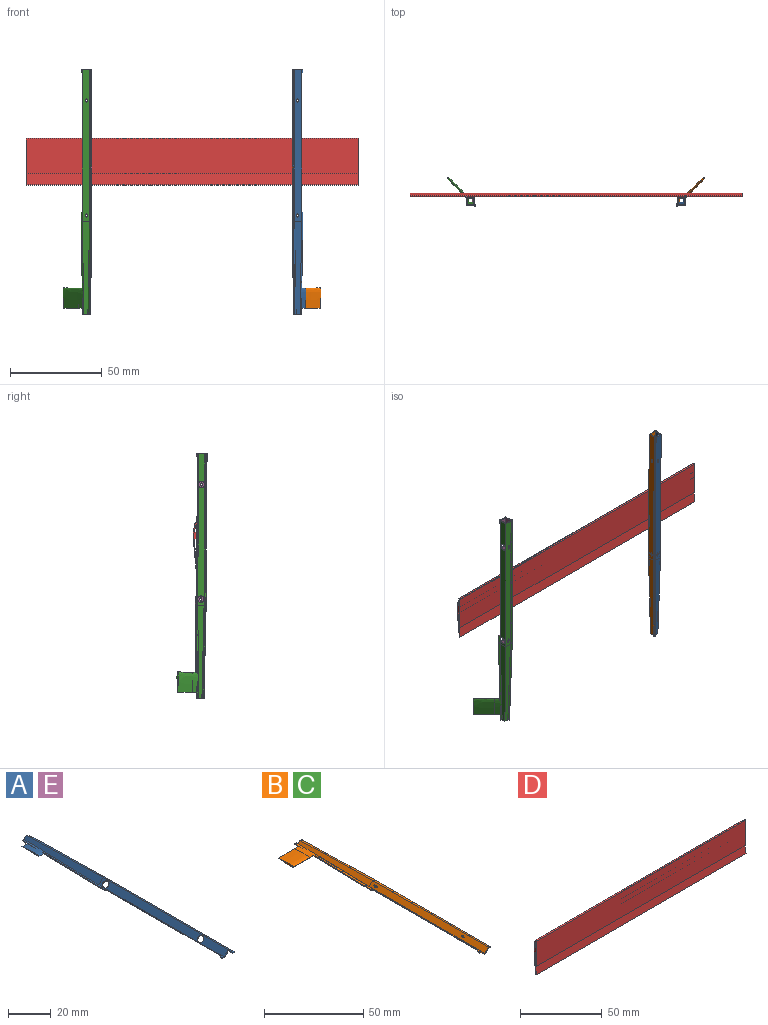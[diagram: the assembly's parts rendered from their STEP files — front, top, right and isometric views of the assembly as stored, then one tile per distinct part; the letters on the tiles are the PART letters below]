
ASSEMBLY  parts=5 mates=2
PART A: 46 faces, bbox 10.2x133.9x3.8 mm
  f0: plane 133.35x4.58mm, normal (0,0,-1), area 117.6mm2, adj f1,f6,f7,f8,f15,f26,f31,f32
  f1: plane 1.46x0.48mm, normal (-1,0,0), area 0.7mm2, adj f0,f3,f15,f38
  f2: plane 43.34x1.86mm, normal (0,0,1), area 40.5mm2, adj f6,f8,f9,f18,f30,f35,f39,f40
  f3: plane 2.67x0.95mm, normal (0,0,1), area 2mm2, adj f1,f9,f15,f38,f42,f43
  f4: cylinder r=1.81mm len=3.63mm, axis (-0.71,0,0.71), area 5.4mm2, adj f7,f9,f19,f37
  f5: plane 9.18x1.18mm, normal (0,0,1), area 8.7mm2, adj f26,f30,f31,f35
  f6: plane 37.73x1.14mm, normal (-1,0.02,0), area 17.5mm2, adj f0,f2,f8,f35
  f7: plane 82.55x2.58mm, normal (0.71,0,-0.71), area 280.9mm2, adj f0,f4,f14,f15,f17,f32
  f8: plane 4.63x0.48mm, normal (-1,0,0), area 2.2mm2, adj f0,f2,f6,f39
  f9: plane 82.55x2.78mm, normal (-0.71,0,0.71), area 303.9mm2, adj f2,f3,f4,f10,f15,f17,f30,f37
  f10: plane 82.55x2.78mm, normal (0.71,0,0.71), area 322mm2, adj f9,f11,f15,f20,f21,f22,f23,f24
  f11: plane 133.35x2.19mm, normal (0,0,1), area 127mm2, adj f10,f12,f15,f26,f28,f29
  f12: plane 82.55x0.48mm, normal (1,0,0), area 39.3mm2, adj f11,f13,f15,f28
  f13: plane 133.35x2.38mm, normal (0,0,-1), area 153.3mm2, adj f12,f14,f15,f26,f27,f28
  f14: plane 82.55x2.58mm, normal (-0.71,0,-0.71), area 299mm2, adj f7,f13,f15,f16,f19,f20,f21,f22
  f15: plane 7.46x3.26mm, normal (0,-1,0), area 4.6mm2, adj f0,f1,f3,f7,f9,f10,f11,f12
  f16: plane 1.1x0.06mm, normal (-0.71,0,0.71), area 0.1mm2, adj f14,f17
  f17: cylinder r=1.81mm len=3.63mm, axis (-0.71,0,0.71), area 5.4mm2, adj f7,f9,f16,f18
  f18: plane 1.1x0.06mm, normal (0.71,0,-0.71), area 0.1mm2, adj f2,f17
  f19: plane 1.1x0.06mm, normal (-0.71,0,0.71), area 0.1mm2, adj f4,f14
  f20: cylinder r=0.19mm len=0.6mm, axis (0.71,0,0.71), area 0.6mm2, adj f10,f14
  f21: cylinder r=0.56mm len=1.13mm, axis (0.71,0,0.71), area 1.7mm2, adj f10,f14
  f22: cylinder r=0.19mm len=0.6mm, axis (0.71,0,0.71), area 0.6mm2, adj f10,f14
  f23: cylinder r=0.19mm len=0.6mm, axis (0.71,0,0.71), area 0.6mm2, adj f10,f14
  f24: cylinder r=0.19mm len=0.6mm, axis (0.71,0,0.71), area 0.6mm2, adj f10,f14
  f25: cylinder r=0.56mm len=1.13mm, axis (0.71,0,0.71), area 1.7mm2, adj f10,f14
  f26: plane 4.99x2.02mm, normal (0,1,0), area 2.9mm2, adj f0,f5,f11,f13,f27,f28,f29,f30
  f27: plane 50.8x2.58mm, normal (-0.71,-0.02,-0.71), area 141.1mm2, adj f13,f14,f26,f32
  f28: plane 50.8x1.23mm, normal (1,0.02,0), area 24.2mm2, adj f11,f12,f13,f26
  f29: plane 50.8x2.78mm, normal (0.71,0.02,0.71), area 155.3mm2, adj f10,f11,f26,f30
  f30: plane 51.37x3.35mm, normal (-0.71,0.02,0.71), area 154.9mm2, adj f2,f5,f9,f26,f29,f35
  f31: plane 9.4x0.7mm, normal (-1,0.02,0), area 3mm2, adj f0,f5,f26,f35
  f32: plane 50.81x2.59mm, normal (0.71,-0.02,-0.71), area 140.5mm2, adj f0,f7,f26,f27,f33,f34
  f33: plane 6.31x0.15mm, normal (1,0,0), area 0.5mm2, adj f0,f32,f34
  f34: extruded ~0.15x0.15mm, area 0mm2, adj f0,f32,f33
  f35: extruded ~11.11x4.16mm, area 40.2mm2, adj f0,f2,f5,f6,f30,f31,f36
  f36: plane 11.11x1.17mm, normal (-1,0,0), area 4mm2, adj f0,f35
  f37: plane 74.2x0.65mm, normal (-1,0,0), area 35.2mm2, adj f0,f4,f9,f41,f42
  f38: cylinder r=0.32mm len=0.48mm, axis (0,0,-1), area 0.1mm2, adj f0,f1,f3,f43
  f39: cylinder r=0.32mm len=0.48mm, axis (0,0,-1), area 0.1mm2, adj f0,f2,f8,f40
  f40: plane 0.77x0.77mm, normal (-0.71,-0.71,0), area 0.5mm2, adj f0,f2,f39,f41
  f41: cylinder r=0.32mm len=0.48mm, axis (0,0,-1), area 0.1mm2, adj f0,f2,f37,f40
  f42: cylinder r=0.32mm len=0.48mm, axis (0,0,-1), area 0.1mm2, adj f0,f3,f37,f43
  f43: plane 0.77x0.77mm, normal (-0.71,0.71,0), area 0.5mm2, adj f0,f3,f38,f42
  f44: cylinder r=0.19mm len=0.48mm, axis (0,0,-1), area 0.6mm2, adj f0,f2
  f45: cylinder r=0.19mm len=0.48mm, axis (0,0,-1), area 0.6mm2, adj f0,f2
PART B: 170 faces, bbox 21.7x133.9x5 mm
  f0: plane 43.34x1.86mm, normal (0,0,-1), area 39.2mm2, adj f7,f9,f12,f13,f21,f89,f90,f91
  f1: plane 9.18x1.18mm, normal (0,0,-1), area 8.3mm2, adj f7,f8,f29,f107,f142,f143,f144,f145
  f2: plane 133.35x2.19mm, normal (0,0,-1), area 122.1mm2, adj f14,f15,f18,f29,f31,f32,f33,f34
  f3: plane 2.67x0.95mm, normal (0,0,-1), area 1.5mm2, adj f5,f13,f18,f82,f83,f84,f85,f86
  f4: plane 133.35x4.58mm, normal (0,0,1), area 117.4mm2, adj f5,f8,f9,f10,f11,f12,f18,f29
  f5: plane 1.46x0.48mm, normal (-1,0,0), area 0.7mm2, adj f3,f4,f18,f112
  f6: cylinder r=1.81mm len=3.63mm, axis (-0.71,0,-0.71), area 5.4mm2, adj f11,f13,f22,f111
  f7: plane 51.37x3.35mm, normal (-0.71,0.02,-0.71), area 154.9mm2, adj f0,f1,f13,f29,f32,f107
  f8: plane 9.4x0.7mm, normal (-1,0.02,0), area 3mm2, adj f1,f4,f29,f107
  f9: plane 37.73x1.14mm, normal (-1,0.02,0), area 17.5mm2, adj f0,f4,f12,f107
  f10: plane 50.81x2.59mm, normal (0.71,-0.02,0.71), area 140.5mm2, adj f4,f11,f29,f30,f105,f106
  f11: plane 82.55x2.58mm, normal (0.71,0,0.71), area 280.9mm2, adj f4,f6,f10,f17,f18,f20
  f12: plane 4.63x0.48mm, normal (-1,0,0), area 2.2mm2, adj f0,f4,f9,f113
  f13: plane 82.55x2.78mm, normal (-0.71,0,-0.71), area 303.9mm2, adj f0,f3,f6,f7,f14,f18,f20,f111
  f14: plane 82.55x2.78mm, normal (0.71,0,-0.71), area 322mm2, adj f2,f13,f18,f23,f24,f25,f26,f27
  f15: plane 82.55x0.48mm, normal (1,0,0), area 39.3mm2, adj f2,f16,f18,f31
  f16: plane 133.35x2.38mm, normal (0,0,1), area 152.5mm2, adj f15,f17,f18,f29,f30,f31,f96,f97
  f17: plane 82.55x2.58mm, normal (-0.71,0,0.71), area 299mm2, adj f11,f16,f18,f19,f22,f23,f24,f25
  f18: plane 7.46x3.26mm, normal (0,-1,0), area 4.6mm2, adj f2,f3,f4,f5,f11,f13,f14,f15
  f19: plane 1.1x0.06mm, normal (-0.71,0,-0.71), area 0.1mm2, adj f17,f20
  f20: cylinder r=1.81mm len=3.63mm, axis (-0.71,0,-0.71), area 5.4mm2, adj f11,f13,f19,f21
  f21: plane 1.1x0.06mm, normal (0.71,0,0.71), area 0.1mm2, adj f0,f20
  f22: plane 1.1x0.06mm, normal (-0.71,0,-0.71), area 0.1mm2, adj f6,f17
  f23: cylinder r=0.19mm len=0.6mm, axis (0.71,0,-0.71), area 0.6mm2, adj f14,f17
  f24: cylinder r=0.56mm len=1.13mm, axis (0.71,0,-0.71), area 1.7mm2, adj f14,f17
  f25: cylinder r=0.19mm len=0.6mm, axis (0.71,0,-0.71), area 0.6mm2, adj f14,f17
  f26: cylinder r=0.19mm len=0.6mm, axis (0.71,0,-0.71), area 0.6mm2, adj f14,f17
  f27: cylinder r=0.19mm len=0.6mm, axis (0.71,0,-0.71), area 0.6mm2, adj f14,f17
  f28: cylinder r=0.56mm len=1.13mm, axis (0.71,0,-0.71), area 1.7mm2, adj f14,f17
  f29: plane 4.99x2.02mm, normal (0,1,0), area 2.9mm2, adj f1,f2,f4,f7,f8,f10,f16,f30
  f30: plane 50.8x2.58mm, normal (-0.71,-0.02,0.71), area 141.1mm2, adj f10,f16,f17,f29
  f31: plane 50.8x1.23mm, normal (1,0.02,0), area 24.2mm2, adj f2,f15,f16,f29
  f32: plane 50.8x2.78mm, normal (0.71,0.02,-0.71), area 155.3mm2, adj f2,f7,f14,f29
  f33: plane 0.43x0.31mm, normal (-1,0,0), area 0.1mm2, adj f2,f34,f38,f39
  f34: plane 0.38x0.31mm, normal (-0.5,0.87,0), area 0.1mm2, adj f2,f33,f35,f39
  f35: plane 0.38x0.31mm, normal (0.5,0.87,0), area 0.1mm2, adj f2,f34,f36,f39
  f36: plane 0.43x0.31mm, normal (1,0,0), area 0.1mm2, adj f2,f35,f37,f39
  f37: plane 0.38x0.31mm, normal (0.5,-0.87,0), area 0.1mm2, adj f2,f36,f38,f39
  f38: plane 0.38x0.31mm, normal (-0.5,-0.87,0), area 0.1mm2, adj f2,f33,f37,f39
  f39: plane 0.87x0.75mm, normal (0,0,-1), area 0.4mm2, adj f33,f34,f35,f36,f37,f38,f96
  f40: plane 0.38x0.31mm, normal (0.5,-0.87,0), area 0.1mm2, adj f2,f41,f45,f46
  f41: plane 0.38x0.31mm, normal (-0.5,-0.87,0), area 0.1mm2, adj f2,f40,f42,f46
  f42: plane 0.43x0.31mm, normal (-1,0,0), area 0.1mm2, adj f2,f41,f43,f46
  f43: plane 0.38x0.31mm, normal (-0.5,0.87,0), area 0.1mm2, adj f2,f42,f44,f46
  f44: plane 0.38x0.31mm, normal (0.5,0.87,0), area 0.1mm2, adj f2,f43,f45,f46
  f45: plane 0.43x0.31mm, normal (1,0,0), area 0.1mm2, adj f2,f40,f44,f46
  f46: plane 0.87x0.75mm, normal (0,0,-1), area 0.4mm2, adj f40,f41,f42,f43,f44,f45,f102
  f47: plane 0.38x0.31mm, normal (0.5,-0.87,0), area 0.1mm2, adj f2,f48,f52,f53
  f48: plane 0.38x0.31mm, normal (-0.5,-0.87,0), area 0.1mm2, adj f2,f47,f49,f53
  f49: plane 0.43x0.31mm, normal (-1,0,0), area 0.1mm2, adj f2,f48,f50,f53
  f50: plane 0.38x0.31mm, normal (-0.5,0.87,0), area 0.1mm2, adj f2,f49,f51,f53
  f51: plane 0.38x0.31mm, normal (0.5,0.87,0), area 0.1mm2, adj f2,f50,f52,f53
  f52: plane 0.43x0.31mm, normal (1,0,0), area 0.1mm2, adj f2,f47,f51,f53
  f53: plane 0.87x0.75mm, normal (0,0,-1), area 0.4mm2, adj f47,f48,f49,f50,f51,f52,f101
  f54: plane 0.38x0.31mm, normal (0.5,-0.87,0), area 0.1mm2, adj f2,f55,f59,f60
  f55: plane 0.38x0.31mm, normal (-0.5,-0.87,0), area 0.1mm2, adj f2,f54,f56,f60
  f56: plane 0.43x0.31mm, normal (-1,0,0), area 0.1mm2, adj f2,f55,f57,f60
  f57: plane 0.38x0.31mm, normal (-0.5,0.87,0), area 0.1mm2, adj f2,f56,f58,f60
  f58: plane 0.38x0.31mm, normal (0.5,0.87,0), area 0.1mm2, adj f2,f57,f59,f60
  f59: plane 0.43x0.31mm, normal (1,0,0), area 0.1mm2, adj f2,f54,f58,f60
  f60: plane 0.87x0.75mm, normal (0,0,-1), area 0.4mm2, adj f54,f55,f56,f57,f58,f59,f100
  f61: plane 0.38x0.31mm, normal (0.5,-0.87,0), area 0.1mm2, adj f2,f62,f66,f67
  f62: plane 0.38x0.31mm, normal (-0.5,-0.87,0), area 0.1mm2, adj f2,f61,f63,f67
  f63: plane 0.43x0.31mm, normal (-1,0,0), area 0.1mm2, adj f2,f62,f64,f67
  f64: plane 0.38x0.31mm, normal (-0.5,0.87,0), area 0.1mm2, adj f2,f63,f65,f67
  f65: plane 0.38x0.31mm, normal (0.5,0.87,0), area 0.1mm2, adj f2,f64,f66,f67
  f66: plane 0.43x0.31mm, normal (1,0,0), area 0.1mm2, adj f2,f61,f65,f67
  f67: plane 0.87x0.75mm, normal (0,0,-1), area 0.4mm2, adj f61,f62,f63,f64,f65,f66,f99
  f68: plane 0.38x0.31mm, normal (0.5,-0.87,0), area 0.1mm2, adj f2,f69,f73,f74
  f69: plane 0.38x0.31mm, normal (-0.5,-0.87,0), area 0.1mm2, adj f2,f68,f70,f74
  f70: plane 0.43x0.31mm, normal (-1,0,0), area 0.1mm2, adj f2,f69,f71,f74
  f71: plane 0.38x0.31mm, normal (-0.5,0.87,0), area 0.1mm2, adj f2,f70,f72,f74
  f72: plane 0.38x0.31mm, normal (0.5,0.87,0), area 0.1mm2, adj f2,f71,f73,f74
  f73: plane 0.43x0.31mm, normal (1,0,0), area 0.1mm2, adj f2,f68,f72,f74
  f74: plane 0.87x0.75mm, normal (0,0,-1), area 0.4mm2, adj f68,f69,f70,f71,f72,f73,f98
  f75: plane 0.38x0.31mm, normal (0.5,-0.87,0), area 0.1mm2, adj f2,f76,f80,f81
  f76: plane 0.38x0.31mm, normal (-0.5,-0.87,0), area 0.1mm2, adj f2,f75,f77,f81
  f77: plane 0.43x0.31mm, normal (-1,0,0), area 0.1mm2, adj f2,f76,f78,f81
  f78: plane 0.38x0.31mm, normal (-0.5,0.87,0), area 0.1mm2, adj f2,f77,f79,f81
  f79: plane 0.38x0.31mm, normal (0.5,0.87,0), area 0.1mm2, adj f2,f78,f80,f81
  f80: plane 0.43x0.31mm, normal (1,0,0), area 0.1mm2, adj f2,f75,f79,f81
  f81: plane 0.87x0.75mm, normal (0,0,-1), area 0.4mm2, adj f75,f76,f77,f78,f79,f80,f97
  f82: plane 0.43x0.31mm, normal (-1,0,0), area 0.1mm2, adj f3,f83,f87,f88
  f83: plane 0.38x0.31mm, normal (-0.5,0.87,0), area 0.1mm2, adj f3,f82,f84,f88
  f84: plane 0.38x0.31mm, normal (0.5,0.87,0), area 0.1mm2, adj f3,f83,f85,f88
  f85: plane 0.43x0.31mm, normal (1,0,0), area 0.1mm2, adj f3,f84,f86,f88
  f86: plane 0.38x0.31mm, normal (0.5,-0.87,0), area 0.1mm2, adj f3,f85,f87,f88
  f87: plane 0.38x0.31mm, normal (-0.5,-0.87,0), area 0.1mm2, adj f3,f82,f86,f88
  f88: plane 0.87x0.75mm, normal (0,0,-1), area 0.4mm2, adj f82,f83,f84,f85,f86,f87,f103
  f89: plane 0.43x0.31mm, normal (-1,0,0), area 0.1mm2, adj f0,f90,f94,f95
  f90: plane 0.38x0.31mm, normal (-0.5,0.87,0), area 0.1mm2, adj f0,f89,f91,f95
  f91: plane 0.38x0.31mm, normal (0.5,0.87,0), area 0.1mm2, adj f0,f90,f92,f95
  f92: plane 0.43x0.31mm, normal (1,0,0), area 0.1mm2, adj f0,f91,f93,f95
  f93: plane 0.38x0.31mm, normal (0.5,-0.87,0), area 0.1mm2, adj f0,f92,f94,f95
  f94: plane 0.38x0.31mm, normal (-0.5,-0.87,0), area 0.1mm2, adj f0,f89,f93,f95
  f95: plane 0.87x0.75mm, normal (0,0,-1), area 0.4mm2, adj f89,f90,f91,f92,f93,f94,f104
  f96: cylinder r=0.19mm len=0.38mm, axis (0,0,-1), area 0.2mm2, adj f16,f39
  f97: cylinder r=0.19mm len=0.38mm, axis (0,0,-1), area 0.2mm2, adj f16,f81
  f98: cylinder r=0.19mm len=0.38mm, axis (0,0,-1), area 0.2mm2, adj f16,f74
  f99: cylinder r=0.19mm len=0.38mm, axis (0,0,-1), area 0.2mm2, adj f16,f67
  f100: cylinder r=0.19mm len=0.38mm, axis (0,0,-1), area 0.2mm2, adj f16,f60
  f101: cylinder r=0.19mm len=0.38mm, axis (0,0,-1), area 0.2mm2, adj f16,f53
  f102: cylinder r=0.19mm len=0.38mm, axis (0,0,-1), area 0.2mm2, adj f16,f46
  f103: cylinder r=0.19mm len=0.38mm, axis (0,0,-1), area 0.2mm2, adj f4,f88
  f104: cylinder r=0.19mm len=0.38mm, axis (0,0,-1), area 0.2mm2, adj f4,f95
  f105: plane 6.31x0.15mm, normal (1,0,0), area 0.5mm2, adj f4,f10,f106
  f106: extruded ~0.15x0.15mm, area 0mm2, adj f4,f10,f105
  f107: extruded ~15.65x11.11mm, area 169.9mm2, adj f0,f1,f4,f7,f8,f9,f108,f109
  f108: extruded ~11.49x11.11mm, area 129.7mm2, adj f107,f109,f110
  f109: plane 11.11x2.34mm, normal (-1,0,0), area 8mm2, adj f107,f108
  f110: plane 11.11x1.17mm, normal (1,0,0), area 4mm2, adj f4,f108
  f111: plane 74.2x0.65mm, normal (-1,0,0), area 35.2mm2, adj f4,f6,f13,f115,f116
  f112: cylinder r=0.32mm len=0.48mm, axis (0,0,-1), area 0.1mm2, adj f3,f4,f5,f117
  f113: cylinder r=0.32mm len=0.48mm, axis (0,0,-1), area 0.1mm2, adj f0,f4,f12,f114
  f114: plane 0.77x0.77mm, normal (-0.71,-0.71,0), area 0.5mm2, adj f0,f4,f113,f115
  f115: cylinder r=0.32mm len=0.48mm, axis (0,0,-1), area 0.1mm2, adj f0,f4,f111,f114
  f116: cylinder r=0.32mm len=0.48mm, axis (0,0,-1), area 0.1mm2, adj f3,f4,f111,f117
  f117: plane 0.77x0.77mm, normal (-0.71,0.71,0), area 0.5mm2, adj f3,f4,f112,f116
  f118: plane 0.38x0.31mm, normal (-0.5,0.87,0), area 0.1mm2, adj f2,f119,f124,f125
  f119: plane 0.38x0.31mm, normal (0.5,0.87,0), area 0.1mm2, adj f2,f118,f120,f125
  f120: plane 0.43x0.31mm, normal (1,0,0), area 0.1mm2, adj f2,f119,f121,f125
  f121: plane 0.38x0.31mm, normal (0.5,-0.87,0), area 0.1mm2, adj f2,f120,f122,f125
  f122: plane 0.38x0.31mm, normal (-0.5,-0.87,0), area 0.1mm2, adj f2,f121,f124,f125
  f123: cylinder r=0.19mm len=0.38mm, axis (0,0,-1), area 0.4mm2, adj f125,f164
  f124: plane 0.43x0.31mm, normal (-1,0,0), area 0.1mm2, adj f2,f118,f122,f125
  f125: plane 0.87x0.75mm, normal (0,0,-1), area 0.4mm2, adj f118,f119,f120,f121,f122,f123,f124
  f126: plane 0.38x0.31mm, normal (-0.5,0.87,0), area 0.1mm2, adj f2,f127,f132,f133
  f127: plane 0.38x0.31mm, normal (0.5,0.87,0), area 0.1mm2, adj f2,f126,f128,f133
  f128: plane 0.43x0.31mm, normal (1,0,0), area 0.1mm2, adj f2,f127,f129,f133
  f129: plane 0.38x0.31mm, normal (0.5,-0.87,0), area 0.1mm2, adj f2,f128,f130,f133
  f130: plane 0.38x0.31mm, normal (-0.5,-0.87,0), area 0.1mm2, adj f2,f129,f132,f133
  f131: cylinder r=0.19mm len=0.38mm, axis (0,0,-1), area 0.4mm2, adj f133,f165
  f132: plane 0.43x0.31mm, normal (-1,0,0), area 0.1mm2, adj f2,f126,f130,f133
  f133: plane 0.87x0.75mm, normal (0,0,-1), area 0.4mm2, adj f126,f127,f128,f129,f130,f131,f132
  f134: plane 0.38x0.31mm, normal (-0.5,0.87,0), area 0.1mm2, adj f2,f135,f140,f141
  f135: plane 0.38x0.31mm, normal (0.5,0.87,0), area 0.1mm2, adj f2,f134,f136,f141
  f136: plane 0.43x0.31mm, normal (1,0,0), area 0.1mm2, adj f2,f135,f137,f141
  f137: plane 0.38x0.31mm, normal (0.5,-0.87,0), area 0.1mm2, adj f2,f136,f138,f141
  f138: plane 0.38x0.31mm, normal (-0.5,-0.87,0), area 0.1mm2, adj f2,f137,f140,f141
  f139: cylinder r=0.19mm len=0.38mm, axis (0,0,-1), area 0.4mm2, adj f141,f166
  f140: plane 0.43x0.31mm, normal (-1,0,0), area 0.1mm2, adj f2,f134,f138,f141
  f141: plane 0.87x0.75mm, normal (0,0,-1), area 0.4mm2, adj f134,f135,f136,f137,f138,f139,f140
  f142: plane 0.38x0.31mm, normal (-0.5,-0.87,0), area 0.1mm2, adj f1,f143,f148,f149
  f143: plane 0.43x0.31mm, normal (-1,0,0), area 0.1mm2, adj f1,f142,f144,f149
  f144: plane 0.38x0.31mm, normal (-0.5,0.87,0), area 0.1mm2, adj f1,f143,f145,f149
  f145: plane 0.38x0.31mm, normal (0.5,0.87,0), area 0.1mm2, adj f1,f144,f146,f149
  f146: plane 0.43x0.31mm, normal (1,0,0), area 0.1mm2, adj f1,f145,f148,f149
  f147: cylinder r=0.19mm len=0.38mm, axis (0,0,-1), area 0.4mm2, adj f149,f167
  f148: plane 0.38x0.31mm, normal (0.5,-0.87,0), area 0.1mm2, adj f1,f142,f146,f149
  f149: plane 0.87x0.75mm, normal (0,0,-1), area 0.4mm2, adj f142,f143,f144,f145,f146,f147,f148
  f150: plane 0.38x0.31mm, normal (-0.5,-0.87,0), area 0.1mm2, adj f0,f151,f155,f156
  f151: plane 0.43x0.31mm, normal (-1,0,0), area 0.1mm2, adj f0,f150,f152,f156
  f152: plane 0.38x0.31mm, normal (-0.5,0.87,0), area 0.1mm2, adj f0,f151,f153,f156
  f153: plane 0.38x0.31mm, normal (0.5,0.87,0), area 0.1mm2, adj f0,f152,f154,f156
  f154: plane 0.43x0.31mm, normal (1,0,0), area 0.1mm2, adj f0,f153,f155,f156
  f155: plane 0.38x0.31mm, normal (0.5,-0.87,0), area 0.1mm2, adj f0,f150,f154,f156
  f156: plane 0.87x0.75mm, normal (0,0,-1), area 0.4mm2, adj f150,f151,f152,f153,f154,f155,f169
  f157: plane 0.38x0.31mm, normal (-0.5,-0.87,0), area 0.1mm2, adj f0,f158,f162,f163
  f158: plane 0.43x0.31mm, normal (-1,0,0), area 0.1mm2, adj f0,f157,f159,f163
  f159: plane 0.38x0.31mm, normal (-0.5,0.87,0), area 0.1mm2, adj f0,f158,f160,f163
  f160: plane 0.38x0.31mm, normal (0.5,0.87,0), area 0.1mm2, adj f0,f159,f161,f163
  f161: plane 0.43x0.31mm, normal (1,0,0), area 0.1mm2, adj f0,f160,f162,f163
  f162: plane 0.38x0.31mm, normal (0.5,-0.87,0), area 0.1mm2, adj f0,f157,f161,f163
  f163: plane 0.87x0.75mm, normal (0,0,-1), area 0.4mm2, adj f157,f158,f159,f160,f161,f162,f168
  f164: plane 0.38x0.38mm, normal (0,0,-1), area 0.1mm2, adj f123
  f165: plane 0.38x0.38mm, normal (0,0,-1), area 0.1mm2, adj f131
  f166: plane 0.38x0.38mm, normal (0,0,-1), area 0.1mm2, adj f139
  f167: plane 0.38x0.38mm, normal (0,0,-1), area 0.1mm2, adj f147
  f168: cylinder r=0.19mm len=0.38mm, axis (0,0,-1), area 0.2mm2, adj f4,f163
  f169: cylinder r=0.19mm len=0.38mm, axis (0,0,-1), area 0.2mm2, adj f4,f156
PART C: same geometry as B
PART D: 17 faces, bbox 181x2x25.6 mm
  f0: cylinder r=0.5mm len=180.98mm, axis (-1,0,0), area 264mm2, adj f1,f14,f15,f16
  f1: plane 180.98x0mm, normal (0,-0.1,1), area 0.5mm2, adj f0,f2,f15,f16
  f2: plane 180.98x18.75mm, normal (0,-1,-0.01), area 3393.3mm2, adj f1,f3,f15,f16
  f3: plane 180.98x10mm, normal (0,1,-0.04), area 1811.1mm2, adj f2,f4,f15,f16
  f4: plane 180.98x0.99mm, normal (0,0,-1), area 178.6mm2, adj f3,f5,f15,f16
  f5: plane 180.98x0.81mm, normal (0,-1,0), area 147mm2, adj f4,f6,f15,f16
  f6: plane 180.98x9.16mm, normal (0,-1,0.1), area 1665.4mm2, adj f5,f7,f15,f16
  f7: plane 180.98x6.35mm, normal (0,-1,0.1), area 1153.9mm2, adj f6,f8,f15,f16
  f8: plane 180.98x0.49mm, normal (0,-0.11,-0.99), area 89.7mm2, adj f7,f9,f15,f16
  f9: plane 180.98x15.53mm, normal (0,1,-0.1), area 2824.2mm2, adj f8,f10,f15,f16
  f10: plane 180.98x4.69mm, normal (0,1,0), area 848.3mm2, adj f9,f14,f15,f16
  f11: plane 180.98x5mm, normal (0,1,0), area 904.9mm2, adj f12,f13,f15,f16
  f12: plane 180.98x4.95mm, normal (0,-0.98,-0.2), area 913.7mm2, adj f11,f13,f15,f16
  f13: plane 180.98x0.99mm, normal (0,-0.05,1), area 178.8mm2, adj f11,f12,f15,f16
  f14: plane 180.98x5mm, normal (0,0.98,0.19), area 922.3mm2, adj f0,f10,f15,f16
  f15: plane 25.62x1.98mm, normal (1,0,0), area 23mm2, adj f0,f1,f2,f3,f4,f5,f6,f7
  f16: plane 25.62x1.98mm, normal (-1,0,0), area 23mm2, adj f0,f1,f2,f3,f4,f5,f6,f7
PART E: same geometry as A
PLACE A rot(axis=(-0.28,0.68,-0.68),148.5deg) t=(15.86,12.64,23.51)mm
PLACE B rot(axis=(-0.28,0.68,-0.68),148.5deg) t=(15.86,12.64,23.51)mm
PLACE C rot(axis=(-0.86,0.36,-0.36),98.1deg) t=(-99.14,12.64,23.51)mm
PLACE D t=(-41.64,16.65,61.04)mm
PLACE E rot(axis=(-0.86,0.36,-0.36),98.1deg) t=(-99.14,12.64,23.51)mm
MATE fastened B.f13 <-> D.f2  axis (0,1,0.01) through (15.51,14.69,65.26)mm
MATE fastened E.f9 <-> D.f2  axis (0,1,0.01) through (-98.79,14.69,65.26)mm
